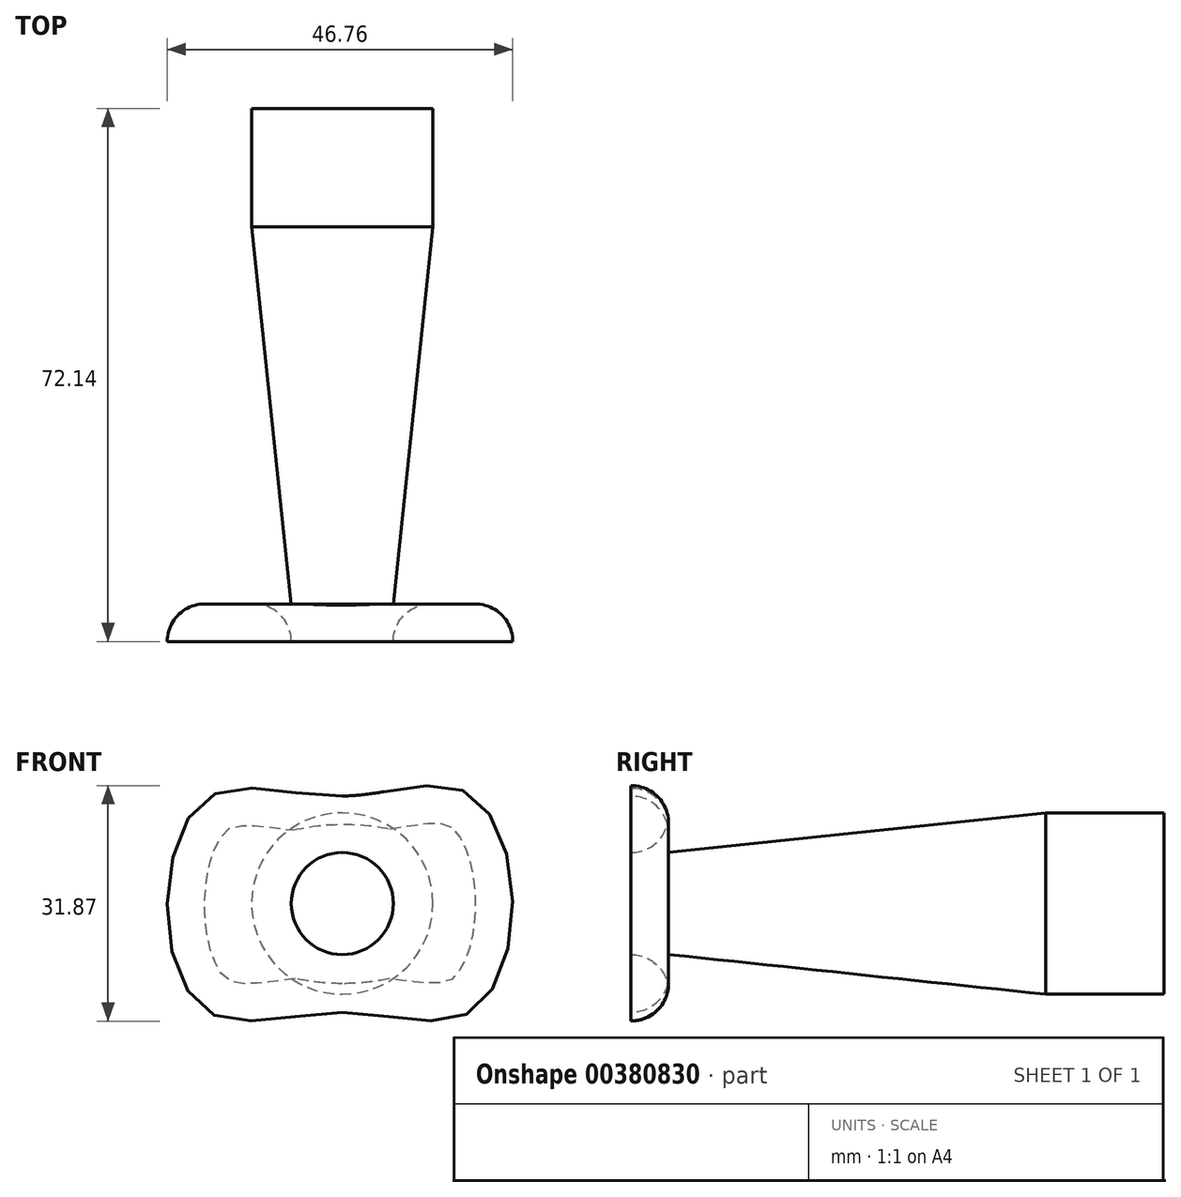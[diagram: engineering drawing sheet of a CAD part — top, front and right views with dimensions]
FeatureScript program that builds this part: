
annotation { "Feature Type Name" : "Feature", "Feature Type Description" : "" }
export const myFeature = defineFeature(function(context is Context, id is Id, definition is map)
    precondition{}
    {
        {
            var Q0;
            Q0=qCreatedBy(makeId("Front.planeOp"),FACE);
            var sketch = newSketch(context, id + "F0", { "sketchPlane" : qUnion([Q0])});
            skCircle(sketch, "E0", {"center": v(0, 0) * mm, "radius": 12.27 * mm});
            skSolve(sketch);
        }
        {
            var Q0;
            Q0=makeQuery(id+"F0.imprint","IMPRINT",FACE,{"disambiguationData":[TD([[makeQuery(id+"F0.imprint","IMPRINT",EDGE,{"derivedFrom":sQuery(id+"F0.wireOp",EDGE,"E0")}),1.0]])]});
            extrude(context, id + "F1", {"entities" : qUnion([Q0]), "depth" : 16 * mm});
        }
        {
            var Q0;
            Q0=makeQuery(id+"F1.opExtrude","CAP_FACE",FACE,{"disambiguationData":[OSD([sQuery(id+"F0.wireOp",EDGE,"E0")])],"isStart":false});
            var sketch = newSketch(context, id + "F2", { "sketchPlane" : qUnion([Q0])});
            skCircle(sketch, "E1", {"center": v(0, 0) * mm, "radius": 12.3 * mm});
            skSolve(sketch);
        }
        {
            var Q0;
            Q0=makeQuery(id+"F2.imprint","IMPRINT",FACE,{"disambiguationData":[TD([[makeQuery(id+"F2.imprint","IMPRINT",EDGE,{"derivedFrom":makeQuery(id+"F1.opExtrude","CAP_EDGE",EDGE,{"disambiguationData":[OSD([sQuery(id+"F0.wireOp",EDGE,"E0")])],"isStart":false})}),1.0]])]});
            var Q1;
            Q1=makeQuery(id+"F1.opExtrude","CAP_FACE",FACE,{"disambiguationData":[OSD([sQuery(id+"F0.wireOp",EDGE,"E0")])],"isStart":true});
            extrude(context, id + "F3", {"entities" : qUnion([Q0, Q1]), "operationType" : NewBodyOperationType.ADD, "depth" : 51.05 * mm, "hasDraft" : true, "draftAngle" : 6 * degree, "draftPullDirection" : true});
        }
        {
            var Q0;
            {var subQ0=sQuery(id+"F0.wireOp",EDGE,"E0");Q0=makeQuery(id+"F3.opExtrude","CAP_FACE",FACE,{"disambiguationData":[OSD([subQ0]),TDD([makeQuery(id+"F2.imprint","IMPRINT",EDGE,{"derivedFrom":makeQuery(id+"F1.opExtrude","CAP_EDGE",EDGE,{"disambiguationData":[OSD([subQ0])],"isStart":false})})])],"isStart":false});}
            var sketch = newSketch(context, id + "F4", { "sketchPlane" : qUnion([Q0])});
            skFitSpline(sketch, "E2", {"points": [v(0, 14.55) * mm, v(-17.46, 14.76) * mm, v(-23.7, 0) * mm, v(-17.66, -14.96) * mm, v(0, -14.76) * mm, v(16.83, -14.96) * mm, v(23.07, 0) * mm, v(16.63, 15.17) * mm, v(0, 14.55) * mm]});
            skSolve(sketch);
        }
        {
            var Q0;
            Q0=makeQuery(id+"F4.imprint","IMPRINT",FACE,{"disambiguationData":[TD([[makeQuery(id+"F4.imprint","IMPRINT",EDGE,{"derivedFrom":sQuery(id+"F4.wireOp",EDGE,"E2")}),1.0]])]});
            extrude(context, id + "F5", {"entities" : qUnion([Q0]), "depth" : 5.08 * mm});
        }
        {
            var Q0;
            Q0=makeQuery(id+"F5.opExtrude","CAP_FACE",FACE,{"disambiguationData":[OSD([sQuery(id+"F0.wireOp",EDGE,"E0"),sQuery(id+"F4.wireOp",EDGE,"E2")])],"isStart":true});
            fillet(context, id + "F6", {"entities" : qUnion([Q0]), "radius" : 5.08 * mm, "tangentPropagation" : true, "allowEdgeOverflow" : false});
        }
    });
